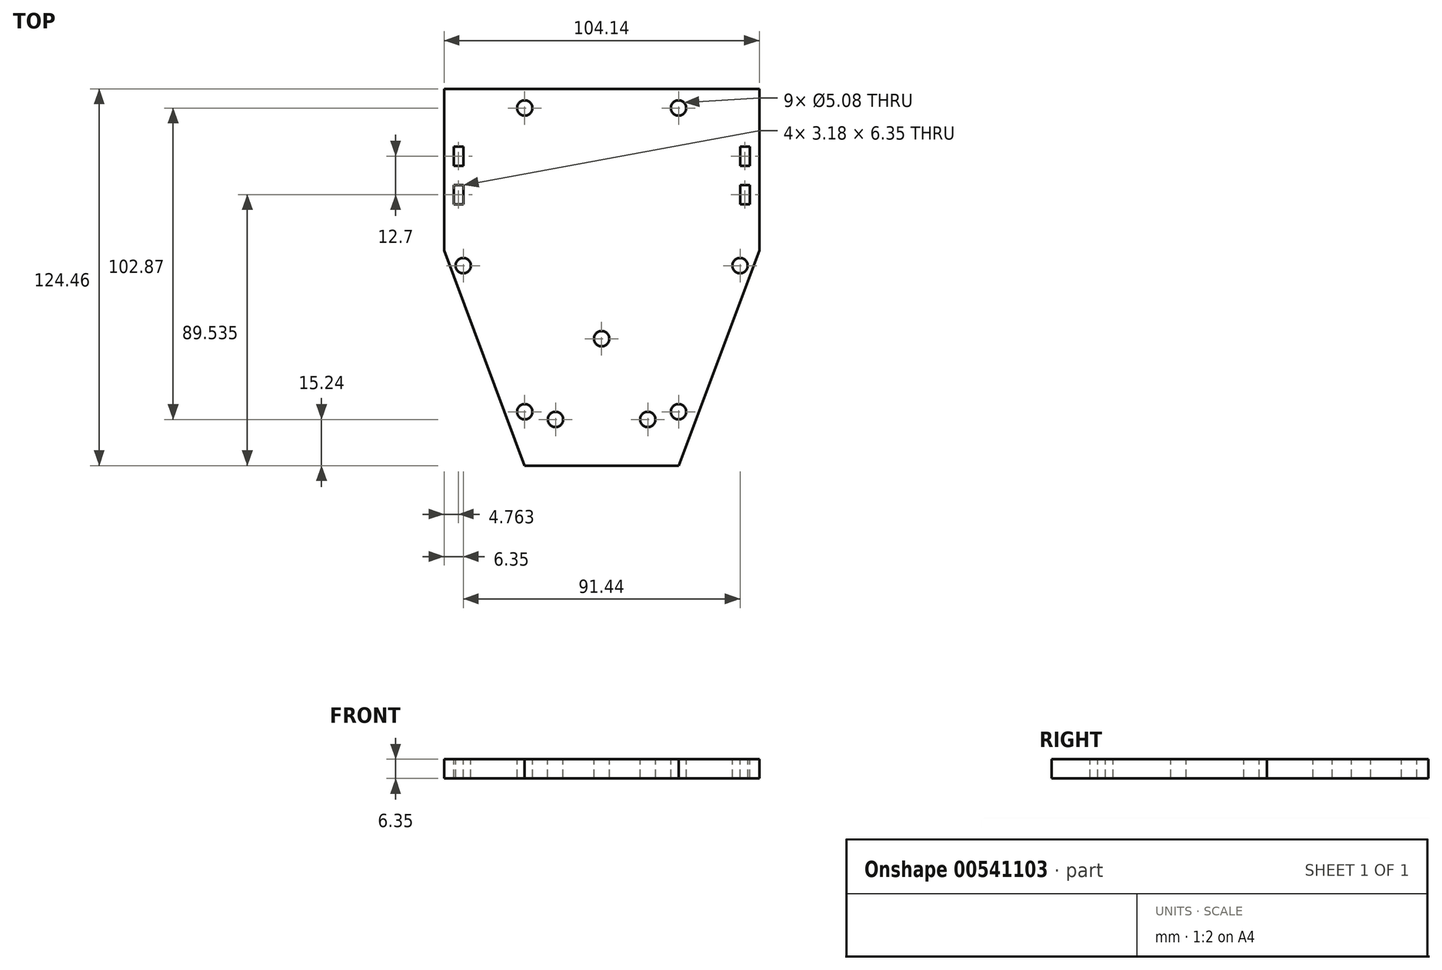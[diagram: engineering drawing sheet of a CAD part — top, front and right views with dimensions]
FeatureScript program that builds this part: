
annotation { "Feature Type Name" : "Feature", "Feature Type Description" : "" }
export const myFeature = defineFeature(function(context is Context, id is Id, definition is map)
    precondition{}
    {
        {
            var Q0;
            Q0=qCreatedBy(makeId("Top.planeOp"),FACE);
            var sketch = newSketch(context, id + "F0", { "sketchPlane" : qUnion([Q0])});
            skLineSegment(sketch, "E0.top", {"start": v(52.07, 82.55) * mm, "end": v(-52.07, 82.55) * mm});
            skLineSegment(sketch, "E0.left", {"start": v(52.07, 29.21) * mm, "end": v(52.07, 82.55) * mm});
            skLineSegment(sketch, "E0.right", {"start": v(-52.07, 29.2) * mm, "end": v(-52.07, 82.55) * mm});
            skPoint(sketch, "E0.middle", {"position": v(0, 55.88) * mm});
            skPoint(sketch, "E1.middle", {"position": v(0, 0) * mm});
            skLineSegment(sketch, "E2", {"start": v(-52.07, 29.21) * mm, "end": v(-25.4, -41.91) * mm});
            skLineSegment(sketch, "E3", {"start": v(52.07, 29.21) * mm, "end": v(25.4, -41.91) * mm});
            skLineSegment(sketch, "E4", {"start": v(0, 55.88) * mm, "end": v(-71.47, 55.88) * mm, "construction": true});
            skLineSegment(sketch, "E5", {"start": v(-25.4, -41.91) * mm, "end": v(0, -41.91) * mm});
            skLineSegment(sketch, "E6", {"start": v(0, -41.91) * mm, "end": v(25.4, -41.91) * mm});
            skLineSegment(sketch, "E7.bottom", {"start": v(-25.4, -41.91) * mm, "end": v(-15.24, -41.91) * mm, "construction": true});
            skLineSegment(sketch, "E7.top", {"start": v(-25.4, -26.67) * mm, "end": v(-15.24, -26.67) * mm, "construction": true});
            skLineSegment(sketch, "E7.left", {"start": v(-25.4, -41.91) * mm, "end": v(-25.4, -26.67) * mm, "construction": true});
            skLineSegment(sketch, "E7.right", {"start": v(-15.24, -41.91) * mm, "end": v(-15.24, -26.67) * mm, "construction": true});
            skPoint(sketch, "E8", {"position": v(-15.24, -26.67) * mm});
            skPoint(sketch, "E9.MirrorP", {"position": v(15.24, -26.67) * mm});
            skSolve(sketch);
        }
        {
            var Q0;
            Q0 = qSketchRegion(id + "F0", true);
            extrude(context, id + "F1", {"entities" : qUnion([Q0]), "depth" : 6.35 * mm, "offsetDistance" : 25.4 * mm});
        }
        {
            var Q0;
            Q0=makeQuery(id+"F1.opExtrude","CAP_FACE",FACE,{"disambiguationData":[OSD([sQuery(id+"F0.wireOp",EDGE,"E0.top"),sQuery(id+"F0.wireOp",EDGE,"E0.left"),sQuery(id+"F0.wireOp",EDGE,"E0.right"),sQuery(id+"F0.wireOp",EDGE,"E2"),sQuery(id+"F0.wireOp",EDGE,"E3"),sQuery(id+"F0.wireOp",EDGE,"E5"),sQuery(id+"F0.wireOp",EDGE,"E6")])],"isStart":false});
            var sketch = newSketch(context, id + "F2", { "sketchPlane" : qUnion([Q0])});
            skPoint(sketch, "E10", {"position": v(0, 0) * mm});
            skLineSegment(sketch, "E11.bottom", {"start": v(-25.4, -41.91) * mm, "end": v(-15.24, -41.91) * mm, "construction": true});
            skLineSegment(sketch, "E11.top", {"start": v(-25.4, -26.67) * mm, "end": v(-15.24, -26.67) * mm, "construction": true});
            skLineSegment(sketch, "E11.left", {"start": v(-25.4, -41.91) * mm, "end": v(-25.4, -26.67) * mm, "construction": true});
            skLineSegment(sketch, "E11.right", {"start": v(-15.24, -41.91) * mm, "end": v(-15.24, -26.67) * mm, "construction": true});
            skPoint(sketch, "E12", {"position": v(-15.24, -26.67) * mm});
            skPoint(sketch, "E13.MirrorP", {"position": v(15.24, -26.67) * mm});
            skLineSegment(sketch, "E14.bottom", {"start": v(-52.07, 29.2) * mm, "end": v(-45.72, 29.2) * mm, "construction": true});
            skLineSegment(sketch, "E14.top", {"start": v(-52.07, 24.13) * mm, "end": v(-45.72, 24.13) * mm, "construction": true});
            skLineSegment(sketch, "E14.left", {"start": v(-52.07, 29.2) * mm, "end": v(-52.07, 24.13) * mm, "construction": true});
            skLineSegment(sketch, "E14.right", {"start": v(-45.72, 29.2) * mm, "end": v(-45.72, 24.13) * mm, "construction": true});
            skLineSegment(sketch, "E15.bottom", {"start": v(0, 82.55) * mm, "end": v(-25.4, 82.55) * mm, "construction": true});
            skLineSegment(sketch, "E15.top", {"start": v(0, 76.2) * mm, "end": v(-25.4, 76.2) * mm, "construction": true});
            skLineSegment(sketch, "E15.left", {"start": v(0, 82.55) * mm, "end": v(0, 76.2) * mm, "construction": true});
            skLineSegment(sketch, "E15.right", {"start": v(-25.4, 82.55) * mm, "end": v(-25.4, 76.2) * mm, "construction": true});
            skLineSegment(sketch, "E16", {"start": v(-25.4, -41.91) * mm, "end": v(-25.4, -24.13) * mm, "construction": true});
            skPoint(sketch, "E17", {"position": v(-25.4, 76.2) * mm});
            skPoint(sketch, "E18", {"position": v(-45.72, 24.13) * mm});
            skPoint(sketch, "E19", {"position": v(-25.4, -24.13) * mm});
            skPoint(sketch, "E20.MirrorP", {"position": v(25.4, 76.2) * mm});
            skPoint(sketch, "E21.MirrorP", {"position": v(45.72, 24.13) * mm});
            skPoint(sketch, "E22.MirrorP", {"position": v(25.4, -24.13) * mm});
            skSolve(sketch);
        }
        {
            var Q0;
            Q0=sQuery(id+"F2.wireOp",VERTEX,"E12");
            var Q1;
            Q1=sQuery(id+"F2.wireOp",VERTEX,"E13.MirrorP");
            var Q2;
            Q2=sQuery(id+"F2.wireOp",VERTEX,"E10");
            var Q3;
            Q3=sQuery(id+"F2.wireOp",VERTEX,"E18");
            var Q4;
            Q4=sQuery(id+"F2.wireOp",VERTEX,"E19");
            var Q5;
            Q5=sQuery(id+"F2.wireOp",VERTEX,"E22.MirrorP");
            var Q6;
            Q6=sQuery(id+"F2.wireOp",VERTEX,"E21.MirrorP");
            var Q7;
            Q7=sQuery(id+"F2.wireOp",VERTEX,"E20.MirrorP");
            var Q8;
            Q8=sQuery(id+"F2.wireOp",VERTEX,"E17");
            var Q9;
            Q9=makeQuery(id+"F1.opExtrude","SWEPT_BODY",BODY,{"disambiguationData":[OSD([sQuery(id+"F0.wireOp",EDGE,"E0.top"),sQuery(id+"F0.wireOp",EDGE,"E0.left"),sQuery(id+"F0.wireOp",EDGE,"E0.right"),sQuery(id+"F0.wireOp",EDGE,"E2"),sQuery(id+"F0.wireOp",EDGE,"E3"),sQuery(id+"F0.wireOp",EDGE,"E5"),sQuery(id+"F0.wireOp",EDGE,"E6")])]});
            hole(context, id + "F3", {"style" : HoleStyle.SIMPLE, "endStyle" : HoleEndStyle.THROUGH, "holeDiameter" : 5.08 * mm, "isTappedThrough" : true, "tappedDepth" : 12.7 * mm, "tapClearance" : 3, "locations" : qUnion([Q0, Q1, Q2, Q3, Q4, Q5, Q6, Q7, Q8]), "scope" : qUnion([Q9])});
        }
        {
            var Q0;
            Q0=makeQuery(id+"F1.opExtrude","CAP_FACE",FACE,{"disambiguationData":[OSD([sQuery(id+"F0.wireOp",EDGE,"E0.top"),sQuery(id+"F0.wireOp",EDGE,"E0.left"),sQuery(id+"F0.wireOp",EDGE,"E0.right"),sQuery(id+"F0.wireOp",EDGE,"E2"),sQuery(id+"F0.wireOp",EDGE,"E3"),sQuery(id+"F0.wireOp",EDGE,"E5"),sQuery(id+"F0.wireOp",EDGE,"E6")])],"isStart":false});
            var sketch = newSketch(context, id + "F4", { "sketchPlane" : qUnion([Q0])});
            skLineSegment(sketch, "E23.bottom", {"start": v(-52.07, 82.55) * mm, "end": v(-48.9, 82.55) * mm, "construction": true});
            skLineSegment(sketch, "E23.top", {"start": v(-52.07, 63.5) * mm, "end": v(-48.9, 63.5) * mm, "construction": true});
            skLineSegment(sketch, "E23.left", {"start": v(-52.07, 82.55) * mm, "end": v(-52.07, 63.5) * mm, "construction": true});
            skLineSegment(sketch, "E23.right", {"start": v(-48.9, 82.55) * mm, "end": v(-48.9, 63.5) * mm, "construction": true});
            skLineSegment(sketch, "E24.bottom", {"start": v(-48.9, 63.5) * mm, "end": v(-45.72, 63.5) * mm});
            skLineSegment(sketch, "E24.top", {"start": v(-48.9, 57.15) * mm, "end": v(-45.72, 57.15) * mm});
            skLineSegment(sketch, "E24.left", {"start": v(-48.9, 63.5) * mm, "end": v(-48.9, 57.15) * mm});
            skLineSegment(sketch, "E24.right", {"start": v(-45.72, 63.5) * mm, "end": v(-45.72, 57.15) * mm});
            skLineSegment(sketch, "E25.MirrorCS", {"start": v(48.9, 63.5) * mm, "end": v(48.9, 57.15) * mm});
            skLineSegment(sketch, "E26.MirrorCS", {"start": v(48.9, 63.5) * mm, "end": v(45.72, 63.5) * mm});
            skLineSegment(sketch, "E27.MirrorCS", {"start": v(48.9, 57.15) * mm, "end": v(45.72, 57.15) * mm});
            skLineSegment(sketch, "E28.MirrorCS", {"start": v(45.72, 63.5) * mm, "end": v(45.72, 57.15) * mm});
            skLineSegment(sketch, "E29", {"start": v(-52.07, 53.98) * mm, "end": v(-35.45, 53.98) * mm, "construction": true});
            skLineSegment(sketch, "E30.MirrorCS", {"start": v(-48.9, 44.45) * mm, "end": v(-48.9, 50.8) * mm});
            skLineSegment(sketch, "E31.MirrorCS", {"start": v(-45.72, 44.45) * mm, "end": v(-45.72, 50.8) * mm});
            skLineSegment(sketch, "E32.MirrorCS", {"start": v(-48.9, 50.8) * mm, "end": v(-45.72, 50.8) * mm});
            skLineSegment(sketch, "E33.MirrorCS", {"start": v(-48.9, 44.45) * mm, "end": v(-45.72, 44.45) * mm});
            skLineSegment(sketch, "E34.MirrorCS", {"start": v(48.9, 44.45) * mm, "end": v(48.9, 50.8) * mm});
            skLineSegment(sketch, "E35.MirrorCS", {"start": v(45.72, 44.45) * mm, "end": v(45.72, 50.8) * mm});
            skLineSegment(sketch, "E36.MirrorCS", {"start": v(48.9, 44.45) * mm, "end": v(45.72, 44.45) * mm});
            skLineSegment(sketch, "E37.MirrorCS", {"start": v(48.9, 50.8) * mm, "end": v(45.72, 50.8) * mm});
            skSolve(sketch);
        }
        {
            var Q0;
            Q0 = qSketchRegion(id + "F4", true);
            extrude(context, id + "F5", {"entities" : qUnion([Q0]), "operationType" : NewBodyOperationType.REMOVE, "oppositeDirection" : true, "depth" : 25.4 * mm, "offsetDistance" : 25.4 * mm});
        }
    });
